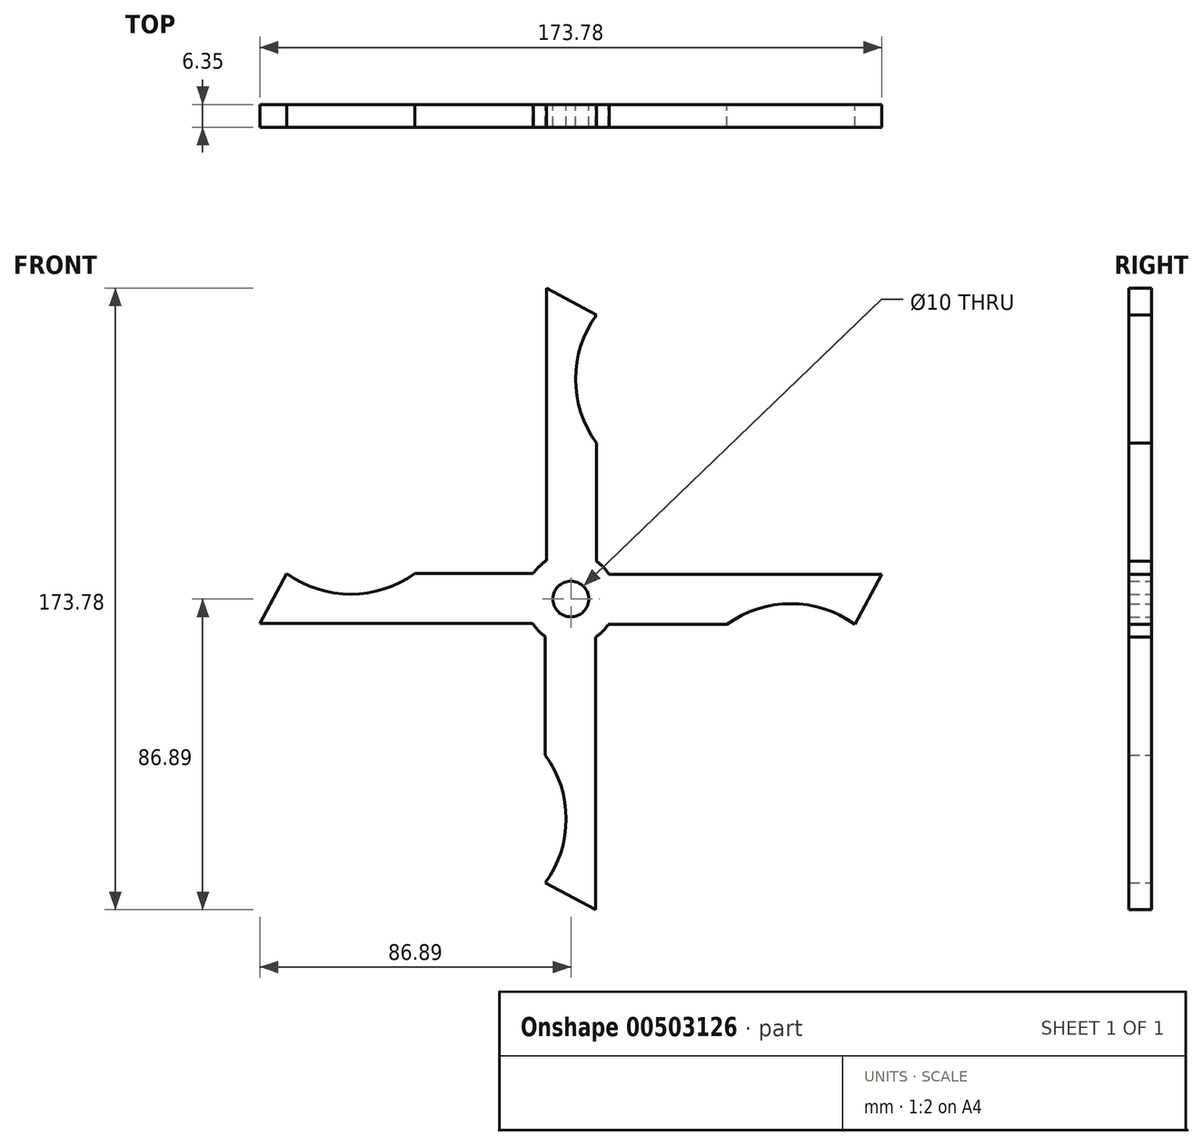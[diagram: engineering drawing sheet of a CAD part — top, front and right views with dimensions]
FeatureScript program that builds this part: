
annotation { "Feature Type Name" : "Feature", "Feature Type Description" : "" }
export const myFeature = defineFeature(function(context is Context, id is Id, definition is map)
    precondition{}
    {
        {
            var Q0;
            Q0=qCreatedBy(makeId("Front.planeOp"),FACE);
            var sketch = newSketch(context, id + "F0", { "sketchPlane" : qUnion([Q0])});
            skCircle(sketch, "E0", {"center": v(0, 0) * mm, "radius": 5 * mm});
            skCircle(sketch, "E1", {"center": v(0, 0) * mm, "radius": 12.7 * mm});
            skLineSegment(sketch, "E2", {"start": v(-6.86, 10.69) * mm, "end": v(-6.86, 86.89) * mm});
            skLineSegment(sketch, "E3", {"start": v(7.13, 10.5) * mm, "end": v(7.13, 43.61) * mm});
            skLineSegment(sketch, "E4.1.0", {"start": v(10.69, 6.86) * mm, "end": v(86.89, 6.86) * mm});
            skLineSegment(sketch, "E4.1.1", {"start": v(86.89, 6.86) * mm, "end": v(79.4, -7.13) * mm});
            skArc(sketch, "E4.1.2", {"start": v(79.4, -7.13) * mm, "mid": v(61.5, -1.33) * mm, "end": v(43.61, -7.13) * mm});
            skLineSegment(sketch, "E4.1.3", {"start": v(10.5, -7.13) * mm, "end": v(43.61, -7.13) * mm});
            skLineSegment(sketch, "E4.2.0", {"start": v(6.86, -10.69) * mm, "end": v(6.86, -86.89) * mm});
            skLineSegment(sketch, "E4.2.1", {"start": v(6.86, -86.89) * mm, "end": v(-7.13, -79.4) * mm});
            skArc(sketch, "E4.2.2", {"start": v(-7.13, -79.4) * mm, "mid": v(-1.33, -61.5) * mm, "end": v(-7.13, -43.61) * mm});
            skLineSegment(sketch, "E4.2.3", {"start": v(-7.13, -10.5) * mm, "end": v(-7.13, -43.61) * mm});
            skLineSegment(sketch, "E5.1.0", {"start": v(-10.69, -6.86) * mm, "end": v(-86.89, -6.86) * mm});
            skLineSegment(sketch, "E5.1.1", {"start": v(-86.89, -6.86) * mm, "end": v(-79.4, 7.13) * mm});
            skArc(sketch, "E5.1.2", {"start": v(-79.4, 7.13) * mm, "mid": v(-61.5, 1.33) * mm, "end": v(-43.61, 7.13) * mm});
            skLineSegment(sketch, "E5.1.3", {"start": v(-10.5, 7.13) * mm, "end": v(-43.61, 7.13) * mm});
            skLineSegment(sketch, "E5.2.1", {"start": v(-6.86, 86.89) * mm, "end": v(7.13, 79.4) * mm});
            skArc(sketch, "E5.2.2", {"start": v(7.13, 79.4) * mm, "mid": v(1.33, 61.5) * mm, "end": v(7.13, 43.61) * mm});
            skSolve(sketch);
        }
        {
            var Q0;
            {var subQ0=sQuery(id+"F0.wireOp",EDGE,"E5.1.0");Q0=makeQuery(id+"F0.imprint","IMPRINT",FACE,{"disambiguationData":[TD([[makeQuery(id+"F0.imprint","IMPRINT",EDGE,{"derivedFrom":subQ0}),-1.0]])]});}
            var Q1;
            {var subQ0=sQuery(id+"F0.wireOp",EDGE,"E4.2.0");Q1=makeQuery(id+"F0.imprint","IMPRINT",FACE,{"disambiguationData":[TD([[makeQuery(id+"F0.imprint","IMPRINT",EDGE,{"derivedFrom":subQ0}),-1.0]])]});}
            var Q2;
            {var subQ0=sQuery(id+"F0.wireOp",EDGE,"E4.1.0");Q2=makeQuery(id+"F0.imprint","IMPRINT",FACE,{"disambiguationData":[TD([[makeQuery(id+"F0.imprint","IMPRINT",EDGE,{"derivedFrom":subQ0}),-1.0]])]});}
            var Q3;
            Q3=makeQuery(id+"F0.imprint","IMPRINT",FACE,{"disambiguationData":[TD([[makeQuery(id+"F0.imprint","IMPRINT",EDGE,{"derivedFrom":sQuery(id+"F0.wireOp",EDGE,"E0")}),-1.0]])]});
            var Q4;
            {var subQ1=sQuery(id+"F0.wireOp",EDGE,"E2");Q4=makeQuery(id+"F0.imprint","IMPRINT",FACE,{"disambiguationData":[TD([[makeQuery(id+"F0.imprint","IMPRINT",EDGE,{"derivedFrom":subQ1}),-1.0]])]});}
            extrude(context, id + "F1", {"entities" : qUnion([Q0, Q1, Q2, Q3, Q4]), "depth" : 6.35 * mm});
        }
    });
